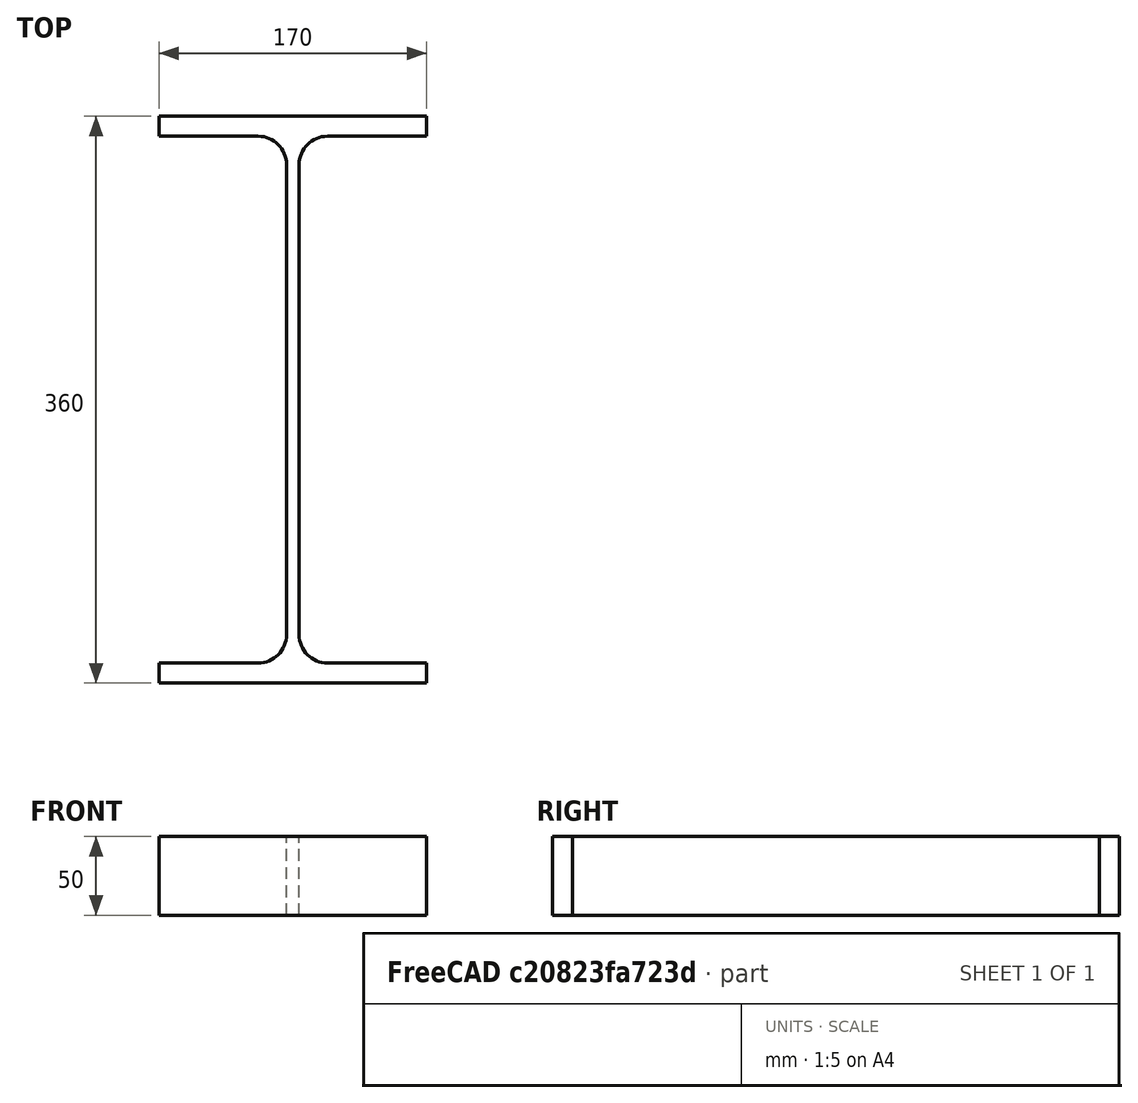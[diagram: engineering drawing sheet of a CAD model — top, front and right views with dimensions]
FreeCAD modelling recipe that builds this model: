
FCSTD DOCUMENT  (FreeCAD 0.15R4671 (Git))
Label: IPE-Profile 360 DIN1025-5 S235JR
License: All rights reserved
LicenseURL: http://en.wikipedia.org/wiki/All_rights_reserved
objects: Sketcher::SketchObject×1, Part::Extrusion×1
note: 2 computed .brp shape members not serialized (recipe doc carries the construction recipe); baked Part::Feature solids carry a one-line shape summary decoded from their .brp

FEATURE [Sketcher::SketchObject] Sketch
  sketch-geometry (16):
    g0: LineSegment StartX=4 StartY=-149.3 StartZ=0 EndX=4 EndY=149.3 EndZ=0
    g1: LineSegment StartX=22 StartY=167.3 StartZ=0 EndX=85 EndY=167.3 EndZ=0
    g2: LineSegment StartX=85 StartY=167.3 StartZ=0 EndX=85 EndY=180 EndZ=0
    g3: LineSegment StartX=85 StartY=180 StartZ=0 EndX=-85 EndY=180 EndZ=0
    g4: LineSegment StartX=-85 StartY=180 StartZ=0 EndX=-85 EndY=167.3 EndZ=0
    g5: LineSegment StartX=-85 StartY=167.3 StartZ=0 EndX=-22 EndY=167.3 EndZ=0
    g6: LineSegment StartX=-4 StartY=149.3 StartZ=0 EndX=-4 EndY=-149.3 EndZ=0
    g7: LineSegment StartX=-22 StartY=-167.3 StartZ=0 EndX=-85 EndY=-167.3 EndZ=0
    g8: LineSegment StartX=-85 StartY=-167.3 StartZ=0 EndX=-85 EndY=-180 EndZ=0
    g9: LineSegment StartX=-85 StartY=-180 StartZ=0 EndX=85 EndY=-180 EndZ=0
    g10: LineSegment StartX=85 StartY=-180 StartZ=0 EndX=85 EndY=-167.3 EndZ=0
    g11: LineSegment StartX=85 StartY=-167.3 StartZ=0 EndX=22 EndY=-167.3 EndZ=0
    g12: ArcOfCircle CenterX=22 CenterY=149.3 CenterZ=0 NormalX=0 NormalY=0 NormalZ=1 Radius=18 StartAngle=1.5708 EndAngle=3.14159
    g13: ArcOfCircle CenterX=22 CenterY=-149.3 CenterZ=0 NormalX=0 NormalY=0 NormalZ=1 Radius=18 StartAngle=3.14159 EndAngle=4.71239
    g14: ArcOfCircle CenterX=-22 CenterY=149.3 CenterZ=0 NormalX=0 NormalY=0 NormalZ=1 Radius=18 StartAngle=0 EndAngle=1.5708
    g15: ArcOfCircle CenterX=-22 CenterY=-149.3 CenterZ=0 NormalX=0 NormalY=0 NormalZ=1 Radius=18 StartAngle=4.71239 EndAngle=6.28319
  constraints (42):
    c: Vertical(g0)
    c: Coincident(g2,g1)
    c: Vertical(g2)
    c: Coincident(g3,g2)
    c: Coincident(g4,g3)
    c: Vertical(g4)
    c: Coincident(g5,g4)
    c: Horizontal(g5)
    c: Vertical(g6)
    c: Horizontal(g7)
    c: Coincident(g8,g7)
    c: Vertical(g8)
    c: Coincident(g9,g8)
    c: Horizontal(g9)
    c: Coincident(g10,g9)
    c: Vertical(g10)
    c: Coincident(g11,g10)
    c: Horizontal(g11)
    c: Tangent(g1,g12) = 1.5708
    c: Tangent(g0,g12) = 1.5708
    c: Tangent(g0,g13) = 1.5708
    c: Tangent(g11,g13) = 1.5708
    c: Tangent(g5,g14) = 1.5708
    c: Tangent(g6,g14) = 1.5708
    c: Tangent(g6,g15) = 1.5708
    c: Tangent(g7,g15) = 1.5708
    c: Equal(g3,g9)
    c: Equal(g2,g4)
    c: Equal(g4,g8)
    c: Equal(g8,g10)
    c: Equal(g12,g14)
    c: Equal(g14,g15)
    c: Equal(g15,g13)
    c: Symmetric(g2,g3,g-2)
    c: Symmetric(g9,g8,g-2)
    c: Symmetric(g0,g6,g-2)
    c: Symmetric(g2,g9,g-1)
    c: DistanceY(g2,g9) = -360
    c: DistanceX(g3) = -170
    c: DistanceX(g0,g6) = -8
    c: DistanceY(g2) = 12.7
    c: Radius(g12) = 18
FEATURE [Part::Extrusion] Extrude  label="IPE-Profile 360 DIN1025-5 S235JR"
  Base = -> Sketch
  Dir = (0,0,50)
  Solid = true
